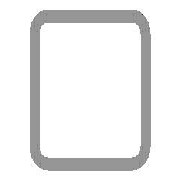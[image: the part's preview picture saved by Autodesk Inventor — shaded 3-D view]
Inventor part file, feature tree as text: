
AUTODESK INVENTOR PART (.ipt)
format: ipt  version: 2025.1 (Build 291241020, 241B)  size: 136,704 bytes
history: native  units: mm (DEFAULTED — no unit token found)
features: other x4, sketch x1, plane x1
ambient origin geometry x8: Origin, YZ Plane, XZ Plane, XY Plane, X Axis, Y Axis, Z Axis, Center Point
bodies: Solid1 (feature_tree), Body (feature_tree)
feature tree (6):
  parser-record x1  (decoder bookkeeping rows leaked as tree rows — omitted from the tree; the rows remain in map.json)
  other  "Driven Length"
  other  "Start plane"
  other  "End plane"
  sketch  "Sketch3"  dims[d3=790.0mm d4=0.0mm d7=6.0mm d9=100.0mm d11=100.0mm d12=3.0mm d13=100.0mm d14=890.0mm d15=50.0mm d16=50.0mm d17=90.0deg d18=790.0mm]
  plane  "Work Plane3"
